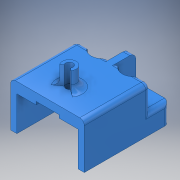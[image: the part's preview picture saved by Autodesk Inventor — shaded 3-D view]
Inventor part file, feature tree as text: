
AUTODESK INVENTOR PART (.ipt)
format: ipt  version: 2018 (Build 220112000, 112)  size: 371,712 bytes
history: native  units: mm
features: extrude x19, sketch x19, projected_geometry x4, mirror x3, fillet x3, plane x1
ambient origin geometry x8: Origin, YZ Plane, XZ Plane, XY Plane, X Axis, Y Axis, Z Axis, Center Point
bodies: Solid1 (feature_tree)
feature tree (49):
  extrude  "Extrusion1"  Depth=24.1mm
  extrude  "Extrusion2"  Depth=27.819mm
  extrude  "Extrusion3"  Depth=2.0mm
  extrude  "Extrusion4"  Depth=2.0mm
  mirror  "Mirror1"
  extrude  "Extrusion6"  Depth=8.2mm
  extrude  "Extrusion7"  Depth=10.95mm
  mirror  "Mirror3"
  extrude  "Extrusion8"  Depth=2.0mm TaperAngle=0.0deg
  mirror  "Mirror4"
  extrude  "Extrusion9"  Depth=4.5mm
  extrude  "Extrusion10"  Depth=2.0mm
  extrude  "Extrusion11"  Depth=4.5mm
  fillet  "Fillet1"  Radius=2.3mm
  fillet  "Fillet2"  Radius=4.5mm
  extrude  "Extrusion12"  Depth=6.1mm
  extrude  "Extrusion13"  Depth=5.0mm TaperAngle=0.0deg
  extrude  "Extrusion14"  Depth=2.0mm
  extrude  "Extrusion16"  Depth=1.5mm TaperAngle=0.0deg
  extrude  "Extrusion17"  Depth=7.4mm
  extrude  "Extrusion18"  Depth=1.0mm TaperAngle=0.0deg
  fillet  "Fillet3"  Radius=1.0mm
  extrude  "Extrusion19"  Depth=6.3mm
  extrude  "Extrusion20"  Depth=1.0mm TaperAngle=0.0deg
  plane  "Work Plane1"
  extrude  "Extrusion22"  Depth=2.0mm
  sketch  "Sketch1"  dims[d0=24.1mm d1=12.05mm]
  sketch  "Sketch2"  dims[d2=27.819mm d3=13.9095mm]
  sketch  "Sketch3"  dims[d4=13.3mm d5=0.0mm d6=2.0mm]
  sketch  "Sketch4"  dims[d7=2.0mm d8=2.0mm]
  sketch  "Sketch6"  dims[d9=10.8mm d10=0.0mm d11=8.2mm]
  sketch  "Sketch7"  dims[d12=10.3mm d13=0.0mm d14=10.95mm]
  sketch  "Sketch8"  dims[d15=2.0mm d16=0.0mm d20=2.0mm d21=0.0mm]
  sketch  "Sketch9"  dims[d22=2.0mm d23=0.0mm d24=4.5mm]
  sketch  "Sketch10"  dims[d27=2.0mm d28=0.0mm d29=6.95mm]
  sketch  "Sketch11"  dims[d30=2.719mm d31=7.13mm d32=2.3mm d33=4.5mm]
  projected_geometry  "Projected Loop1"
  sketch  "Sketch12"  dims[d34=6.1mm d35=0.0mm d36=6.108652mm]
  sketch  "Sketch13"  dims[d37=6.108652mm d38=5.0mm d39=0.0mm]
  sketch  "Sketch14"  dims[d40=5.0mm d41=0.0mm d42=2.0mm]
  sketch  "Sketch16"  dims[d43=1.5mm d44=5.0mm d45=0.0mm]
  projected_geometry  "Projected Loop2"
  sketch  "Sketch17"  dims[d46=7.4mm d47=7.4mm]
  sketch  "Sketch18"  dims[d48=5.0mm d49=0.0mm d50=5.0mm d51=0.0mm d54=1.0mm d55=0.0mm]
  sketch  "Sketch19"  dims[d57=7.5mm d58=6.3mm]
  sketch  "Sketch20"  dims[d59=17.0mm d60=1.0mm d61=0.0mm]
  projected_geometry  "Projected Loop3"
  sketch  "Sketch22"  dims[d62=1.0mm d63=0.0mm d64=2.0mm d65=2.45mm d66=10.0mm d67=0.0mm d68=1.0mm d69=0.0mm d70=2.0mm d74=0.5mm d75=0.0mm]
  projected_geometry  "Projected Loop4"
